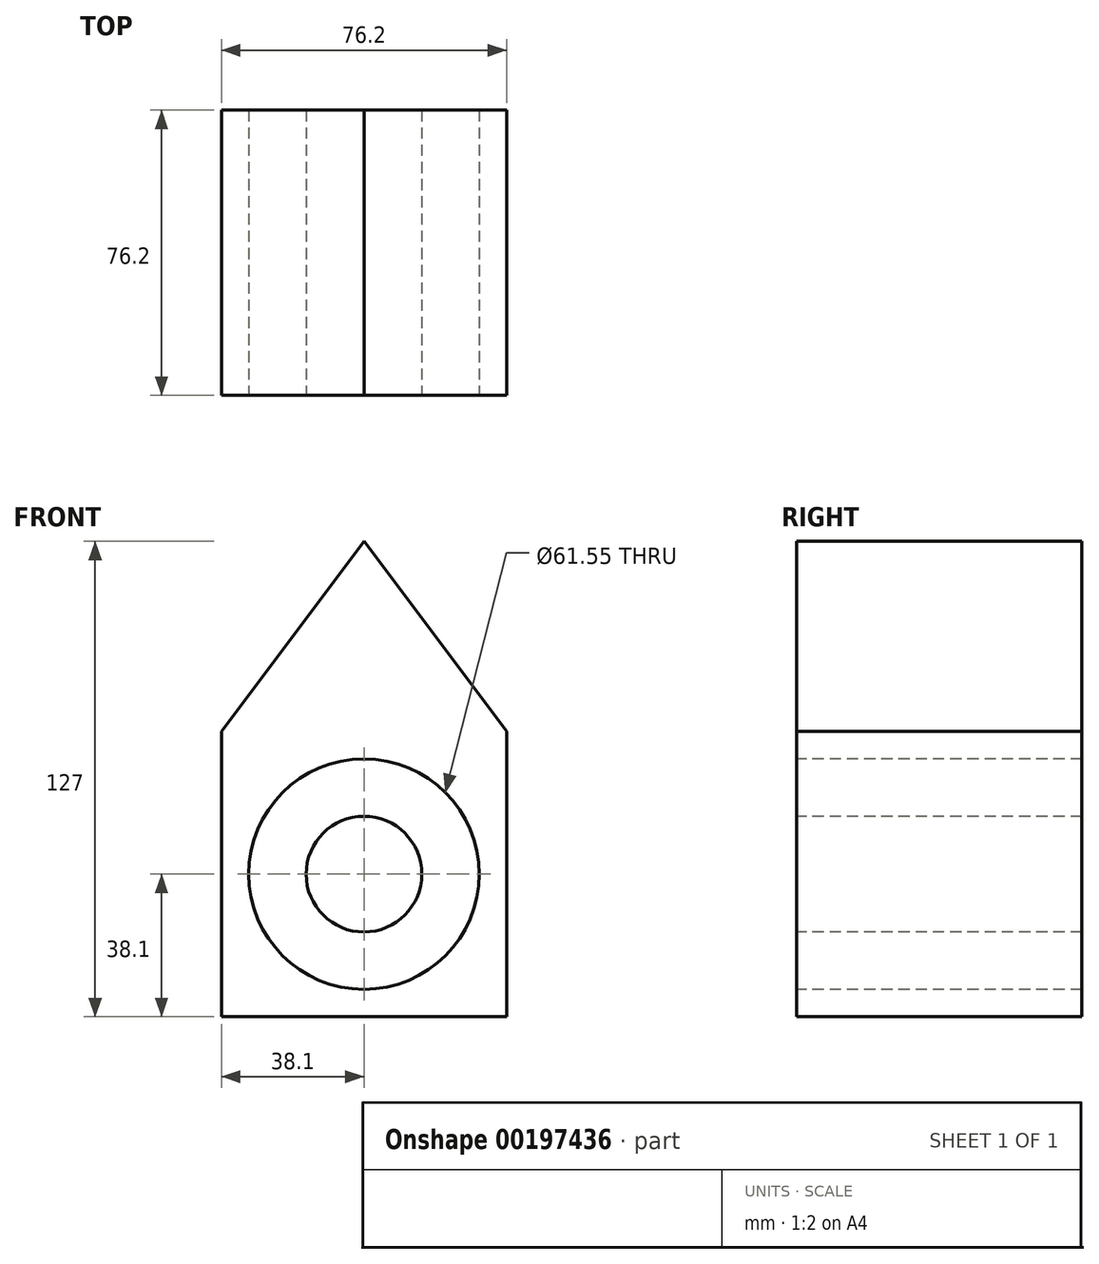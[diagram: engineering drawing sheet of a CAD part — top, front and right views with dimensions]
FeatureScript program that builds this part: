
annotation { "Feature Type Name" : "Feature", "Feature Type Description" : "" }
export const myFeature = defineFeature(function(context is Context, id is Id, definition is map)
    precondition{}
    {
        {
            var Q0;
            Q0=qCreatedBy(makeId("Front.planeOp"),FACE);
            var sketch = newSketch(context, id + "F0", { "sketchPlane" : qUnion([Q0])});
            skLineSegment(sketch, "E0.bottom", {"start": v(-38.1, 38.1) * mm, "end": v(38.1, 38.1) * mm});
            skLineSegment(sketch, "E0.top", {"start": v(-38.1, -38.1) * mm, "end": v(38.1, -38.1) * mm});
            skLineSegment(sketch, "E0.left", {"start": v(-38.1, 38.1) * mm, "end": v(-38.1, -38.1) * mm});
            skLineSegment(sketch, "E0.right", {"start": v(38.1, 38.1) * mm, "end": v(38.1, -38.1) * mm});
            skLineSegment(sketch, "E1", {"start": v(-38.1, 38.1) * mm, "end": v(0, 88.9) * mm});
            skLineSegment(sketch, "E2", {"start": v(0, 88.9) * mm, "end": v(38.1, 38.1) * mm});
            skSolve(sketch);
        }
        {
            var Q0;
            Q0 = qSketchRegion(id + "F0", true);
            extrude(context, id + "F1", {"entities" : qUnion([Q0]), "depth" : 76.2 * mm});
        }
        {
            var Q0;
            Q0=makeQuery(id+"F1.opExtrude","CAP_FACE",FACE,{"disambiguationData":[OSD([sQuery(id+"F0.wireOp",EDGE,"E0.top"),sQuery(id+"F0.wireOp",EDGE,"E0.left"),sQuery(id+"F0.wireOp",EDGE,"E0.right"),sQuery(id+"F0.wireOp",EDGE,"E1"),sQuery(id+"F0.wireOp",EDGE,"E2")])],"isStart":false});
            var sketch = newSketch(context, id + "F2", { "sketchPlane" : qUnion([Q0])});
            skCircle(sketch, "E3", {"center": v(0, 0) * mm, "radius": 15.45 * mm});
            skCircle(sketch, "E4", {"center": v(0, 0) * mm, "radius": 30.78 * mm});
            skSolve(sketch);
        }
        {
            var Q0;
            Q0 = qSketchRegion(id + "F2", true);
            extrude(context, id + "F3", {"entities" : qUnion([Q0]), "operationType" : NewBodyOperationType.REMOVE, "endBound" : BoundingType.THROUGH_ALL, "oppositeDirection" : true, "depth" : 76.2 * mm});
        }
    });
